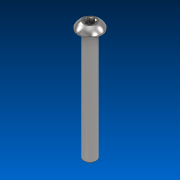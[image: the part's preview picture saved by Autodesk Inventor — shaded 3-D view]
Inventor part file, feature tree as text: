
AUTODESK INVENTOR PART (.ipt)
format: ipt  version: 2022.2 (Build 262287000, 287)  size: 165,888 bytes
history: native  units: in
note: dims shown in document units (in); Inventor stores cm internally (conversion verified against a paired STEP export)
features: direct_edit x1, chamfer x1, move_body x1
ambient origin geometry x8: Origin, YZ Plane, XZ Plane, XY Plane, X Axis, Y Axis, Z Axis, Center Point
bodies: Solid1 (feature_tree)
feature tree (3):
  direct_edit  "Direct Edit1"
  chamfer  "Chamfer2"  [1 undecoded]
  move_body  "Move1"
note: 1 required parameter value undecoded (feature->parameter linkage not recoverable at this tier; creation-order binding heuristic only, values carry confidence <= 0.55)
